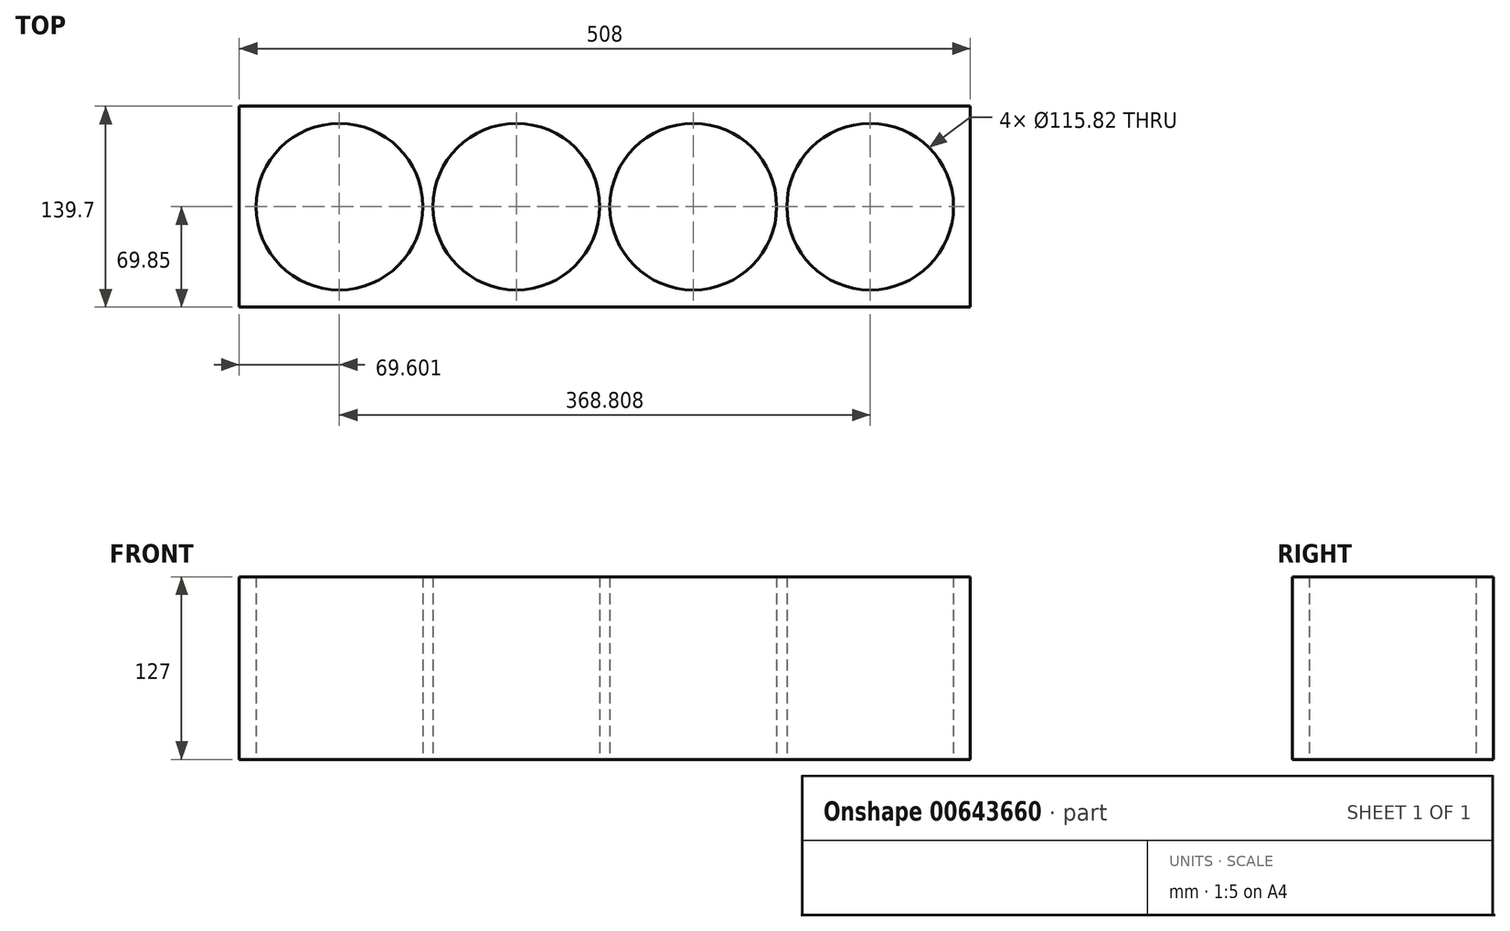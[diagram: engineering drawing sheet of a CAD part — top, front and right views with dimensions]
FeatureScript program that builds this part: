
annotation { "Feature Type Name" : "Feature", "Feature Type Description" : "" }
export const myFeature = defineFeature(function(context is Context, id is Id, definition is map)
    precondition{}
    {
        {
            var Q0;
            Q0=qCreatedBy(makeId("Top.planeOp"),FACE);
            var sketch = newSketch(context, id + "F0", { "sketchPlane" : qUnion([Q0])});
            skCircle(sketch, "E0", {"center": v(-191.05, 0) * mm, "radius": 57.91 * mm});
            skCircle(sketch, "E1.1.0.0", {"center": v(-68.11, 0) * mm, "radius": 57.91 * mm});
            skCircle(sketch, "E1.2.0.0", {"center": v(54.82, 0) * mm, "radius": 57.91 * mm});
            skCircle(sketch, "E1.3.0.0", {"center": v(177.76, 0) * mm, "radius": 57.91 * mm});
            skLineSegment(sketch, "E1.direction1", {"start": v(-191.05, 0) * mm, "end": v(-68.11, 0) * mm, "construction": true});
            skLineSegment(sketch, "E2", {"start": v(-134.92, 0) * mm, "end": v(177.76, 0) * mm, "construction": true});
            skLineSegment(sketch, "E3.bottom", {"start": v(247.35, 69.85) * mm, "end": v(-260.65, 69.85) * mm});
            skLineSegment(sketch, "E3.left", {"start": v(247.35, 69.85) * mm, "end": v(247.35, -69.85) * mm});
            skLineSegment(sketch, "E3.right", {"start": v(-260.65, 69.85) * mm, "end": v(-260.65, -69.85) * mm});
            skPoint(sketch, "E3.middle", {"position": v(-6.65, 0) * mm});
            skLineSegment(sketch, "E4", {"start": v(-260.65, -69.85) * mm, "end": v(247.35, -69.85) * mm});
            skSolve(sketch);
        }
        {
            var Q0;
            Q0=makeQuery(id+"F0.imprint","IMPRINT",FACE,{"disambiguationData":[TD([[makeQuery(id+"F0.imprint","IMPRINT",EDGE,{"derivedFrom":sQuery(id+"F0.wireOp",EDGE,"E0")}),-1.0]])]});
            extrude(context, id + "F1", {"entities" : qUnion([Q0]), "depth" : 127 * mm, "offsetDistance" : 25.4 * mm});
        }
    });
